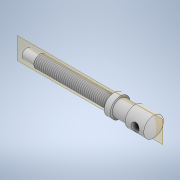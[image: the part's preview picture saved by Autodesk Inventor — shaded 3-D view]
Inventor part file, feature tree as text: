
AUTODESK INVENTOR PART (.ipt)
format: ipt  version: 2021 (Build 250183000, 183)  size: 144,896 bytes
history: native  units: mm
features: other x2, sketch x2, thread x1, extrude x1
ambient origin geometry x8: Origin, YZ Plane, XZ Plane, XY Plane, X Axis, Y Axis, Z Axis, Center Point
bodies: Body1 (feature_tree)
feature tree (6):
  other  "Sólido1"
  other  "Revolução1"
  thread  "Rosca1"  [1 undecoded]
  extrude  "Extrusão1"  Depth=1.25mm
  sketch  "Esboço1"  dims[d15=10.297443mm d17=1.25mm]
  sketch  "Esboço3"  dims[d19=3.0mm d20=5.0mm d21=12.0mm d22=15.0mm d24=13.0mm d25=1.5mm d26=7.5mm d27=90.0deg d28=65.0mm d29=0.0mm d30=6.5mm d34=7.0mm d35=8.0mm d36=0.0mm d37=34.0mm d33=0.5mm]
note: 1 required parameter value undecoded (feature->parameter linkage not recoverable at this tier; creation-order binding heuristic only, values carry confidence <= 0.55)
